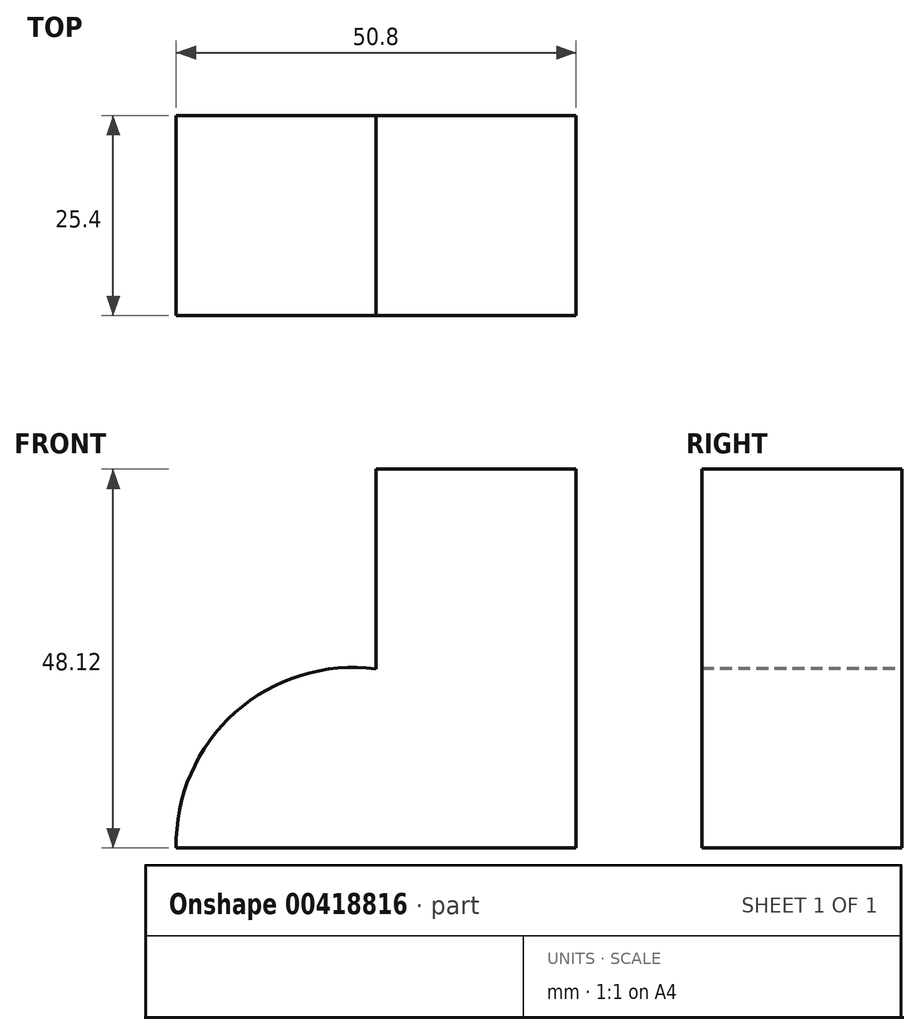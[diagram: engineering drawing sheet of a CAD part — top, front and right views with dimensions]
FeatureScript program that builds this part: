
annotation { "Feature Type Name" : "Feature", "Feature Type Description" : "" }
export const myFeature = defineFeature(function(context is Context, id is Id, definition is map)
    precondition{}
    {
        {
            var Q0;
            Q0=qCreatedBy(makeId("Front.planeOp"),FACE);
            var sketch = newSketch(context, id + "F0", { "sketchPlane" : qUnion([Q0])});
            skLineSegment(sketch, "E0", {"start": v(0, 0) * mm, "end": v(-50.8, 0) * mm});
            skArc(sketch, "E1", {"start": v(-25.4, 22.72) * mm, "mid": v(-43.32, 17.2) * mm, "end": v(-50.8, 0) * mm});
            skLineSegment(sketch, "E2", {"start": v(-25.4, 22.72) * mm, "end": v(-25.4, 48.12) * mm});
            skLineSegment(sketch, "E3", {"start": v(-25.4, 48.12) * mm, "end": v(0, 48.12) * mm});
            skLineSegment(sketch, "E4", {"start": v(0, 48.12) * mm, "end": v(0, 0) * mm});
            skSolve(sketch);
        }
        {
            var Q0;
            Q0 = qSketchRegion(id + "F0", true);
            extrude(context, id + "F1", {"entities" : qUnion([Q0]), "depth" : 25.4 * mm});
        }
    });
